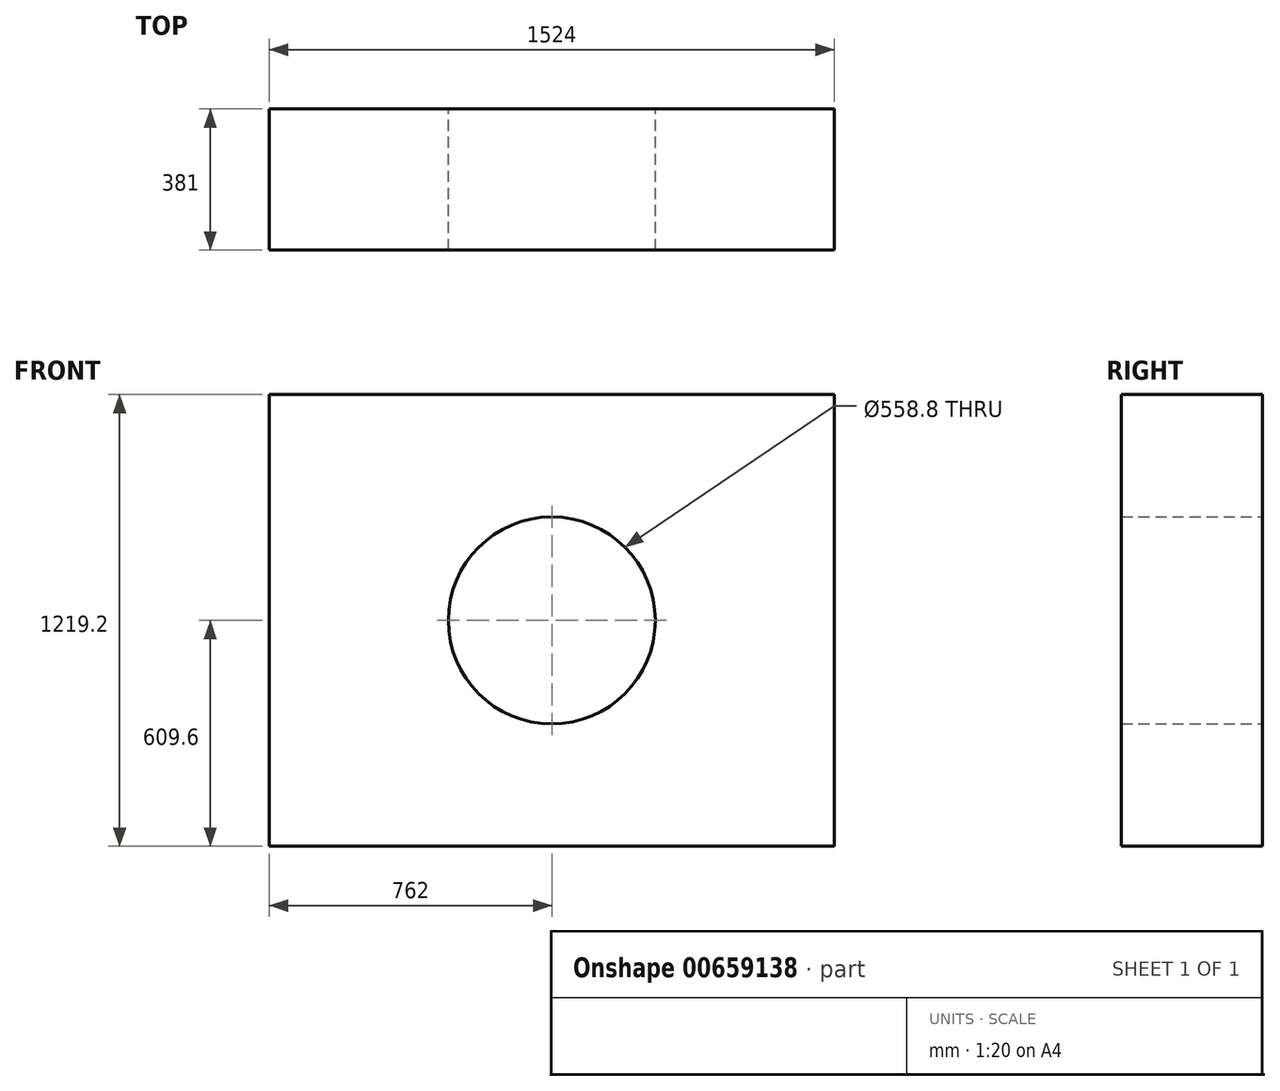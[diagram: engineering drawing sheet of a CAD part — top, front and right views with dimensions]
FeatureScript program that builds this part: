
annotation { "Feature Type Name" : "Feature", "Feature Type Description" : "" }
export const myFeature = defineFeature(function(context is Context, id is Id, definition is map)
    precondition{}
    {
        {
            var Q0;
            Q0=qCreatedBy(makeId("Front.planeOp"),FACE);
            var sketch = newSketch(context, id + "F0", { "sketchPlane" : qUnion([Q0])});
            skLineSegment(sketch, "E0.bottom", {"start": v(0, 0) * mm, "end": v(1524, 0) * mm});
            skLineSegment(sketch, "E0.top", {"start": v(0, 1219.2) * mm, "end": v(1524, 1219.2) * mm});
            skLineSegment(sketch, "E0.left", {"start": v(0, 0) * mm, "end": v(0, 1219.2) * mm});
            skLineSegment(sketch, "E0.right", {"start": v(1524, 0) * mm, "end": v(1524, 1219.2) * mm});
            skCircle(sketch, "E1", {"center": v(762, 609.6) * mm, "radius": 279.4 * mm});
            skSolve(sketch);
        }
        {
            var Q0;
            Q0 = qSketchRegion(id + "F0", true);
            extrude(context, id + "F1", {"entities" : qUnion([Q0]), "depth" : 381 * mm, "offsetDistance" : 25.4 * mm});
        }
    });
